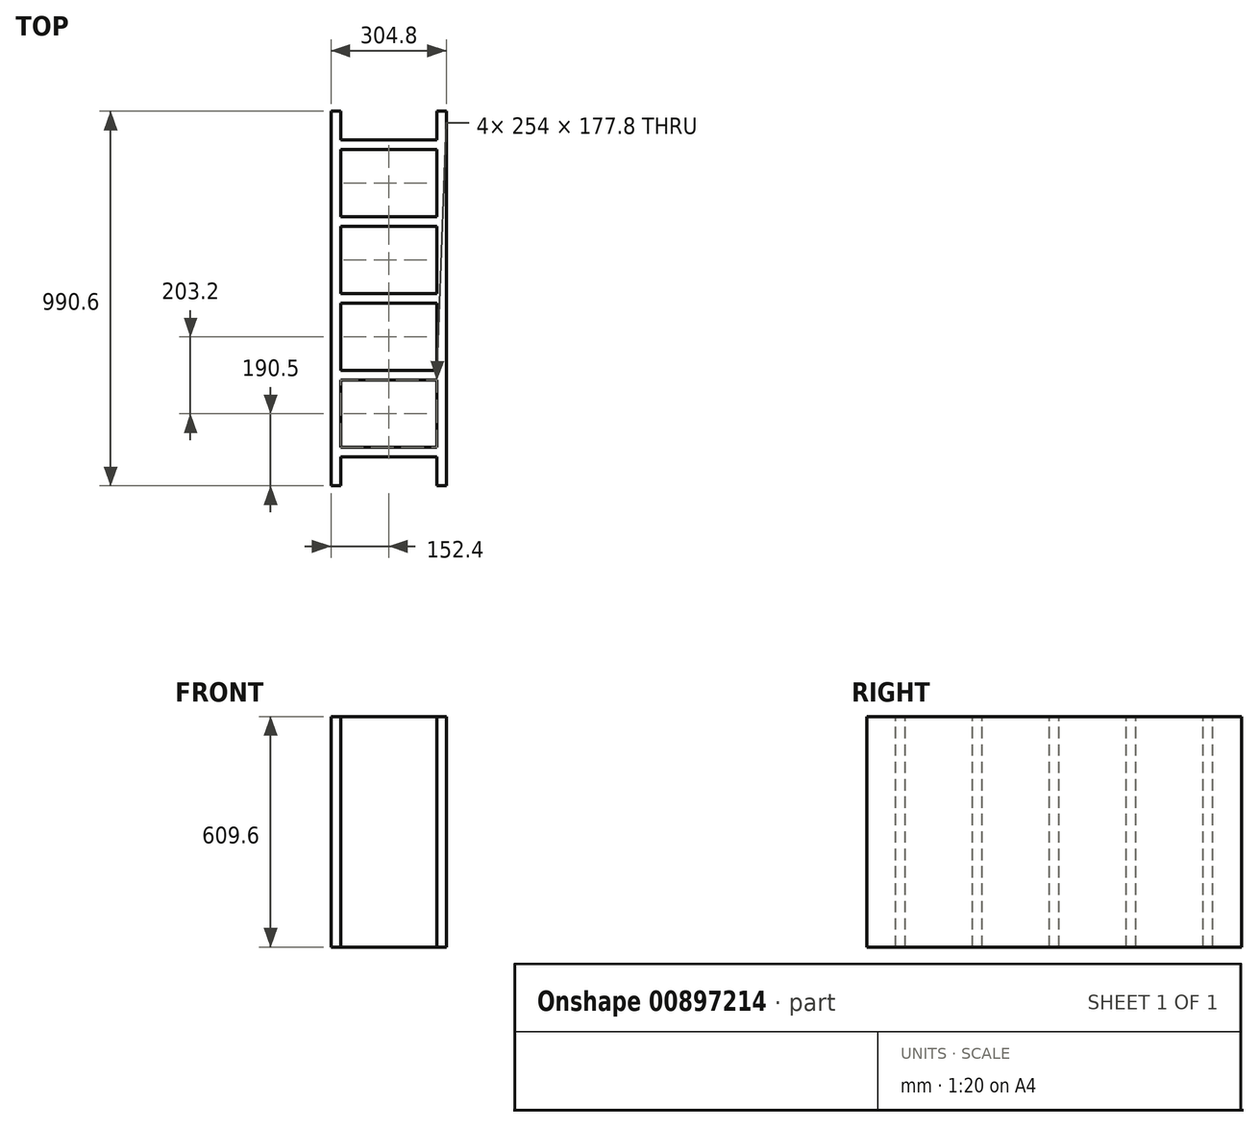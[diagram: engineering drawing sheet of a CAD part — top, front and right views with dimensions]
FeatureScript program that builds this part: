
annotation { "Feature Type Name" : "Feature", "Feature Type Description" : "" }
export const myFeature = defineFeature(function(context is Context, id is Id, definition is map)
    precondition{}
    {
        {
            var Q0;
            Q0=qCreatedBy(makeId("Top.planeOp"),FACE);
            var sketch = newSketch(context, id + "F0", { "sketchPlane" : qUnion([Q0])});
            skLineSegment(sketch, "E0.top", {"start": v(0, 838.2) * mm, "end": v(304.8, 838.2) * mm});
            skLineSegment(sketch, "E0.left", {"start": v(0, 419.1) * mm, "end": v(0, 838.2) * mm});
            skLineSegment(sketch, "E0.right", {"start": v(304.8, 419.1) * mm, "end": v(304.8, 431.8) * mm});
            skLineSegment(sketch, "E1", {"start": v(25.4, 812.8) * mm, "end": v(304.8, 812.8) * mm});
            skLineSegment(sketch, "E2", {"start": v(0, 419.1) * mm, "end": v(416.46, 419.1) * mm, "construction": true});
            skLineSegment(sketch, "E3", {"start": v(25.4, 812.8) * mm, "end": v(25.4, 635) * mm});
            skLineSegment(sketch, "E4", {"start": v(25.4, 431.8) * mm, "end": v(304.8, 431.8) * mm});
            skPoint(sketch, "E0.bottom.start.orphan", {"position": v(0, 0) * mm});
            skLineSegment(sketch, "E5.trimOffspring", {"start": v(304.8, 812.8) * mm, "end": v(304.8, 838.2) * mm});
            skLineSegment(sketch, "E6.MirrorCS", {"start": v(304.8, 25.4) * mm, "end": v(304.8, 0) * mm});
            skLineSegment(sketch, "E7.MirrorCS", {"start": v(304.8, 419.1) * mm, "end": v(304.8, 406.4) * mm});
            skLineSegment(sketch, "E8.MirrorCS", {"start": v(25.4, 25.4) * mm, "end": v(304.8, 25.4) * mm});
            skLineSegment(sketch, "E9.MirrorCS", {"start": v(0, 0) * mm, "end": v(304.8, 0) * mm});
            skLineSegment(sketch, "E10.MirrorCS", {"start": v(25.4, 406.4) * mm, "end": v(304.8, 406.4) * mm});
            skLineSegment(sketch, "E11.MirrorCS", {"start": v(25.4, 25.4) * mm, "end": v(25.4, 203.2) * mm});
            skLineSegment(sketch, "E12.MirrorCS", {"start": v(0, 419.1) * mm, "end": v(0, 0) * mm});
            skPoint(sketch, "E13.orphan", {"position": v(25.4, 419.1) * mm});
            skLineSegment(sketch, "E14.0.1.0", {"start": v(25.4, 635) * mm, "end": v(304.8, 635) * mm});
            skLineSegment(sketch, "E14.0.1.1", {"start": v(304.8, 622.3) * mm, "end": v(304.8, 635) * mm});
            skLineSegment(sketch, "E14.0.1.2", {"start": v(304.8, 622.3) * mm, "end": v(304.8, 609.6) * mm});
            skLineSegment(sketch, "E14.0.1.3", {"start": v(25.4, 609.6) * mm, "end": v(304.8, 609.6) * mm});
            skLineSegment(sketch, "E14.direction1", {"start": v(25.4, 431.8) * mm, "end": v(50.8, 431.8) * mm, "construction": true});
            skLineSegment(sketch, "E14.direction2", {"start": v(25.4, 431.8) * mm, "end": v(25.4, 609.6) * mm, "construction": true});
            skLineSegment(sketch, "E15.trimOffspring", {"start": v(25.4, 609.6) * mm, "end": v(25.4, 431.8) * mm});
            skLineSegment(sketch, "E16.MirrorCS", {"start": v(25.4, 203.2) * mm, "end": v(304.8, 203.2) * mm});
            skLineSegment(sketch, "E17.MirrorCS", {"start": v(25.4, 228.6) * mm, "end": v(304.8, 228.6) * mm});
            skLineSegment(sketch, "E18.MirrorCS", {"start": v(304.8, 215.9) * mm, "end": v(304.8, 203.2) * mm});
            skLineSegment(sketch, "E19.MirrorCS", {"start": v(304.8, 215.9) * mm, "end": v(304.8, 228.6) * mm});
            skLineSegment(sketch, "E20.trimOffspring", {"start": v(25.4, 228.6) * mm, "end": v(25.4, 406.4) * mm});
            skSolve(sketch);
        }
        {
            var Q0;
            Q0 = qSketchRegion(id + "F0", true);
            extrude(context, id + "F1", {"entities" : qUnion([Q0]), "oppositeDirection" : true, "depth" : 609.6 * mm, "offsetDistance" : 25.4 * mm});
        }
        {
            var Q0;
            Q0=makeQuery(id+"F0.imprint","IMPRINT",FACE,{"disambiguationData":[TD([[makeQuery(id+"F0.imprint","IMPRINT",EDGE,{"derivedFrom":sQuery(id+"F0.wireOp",EDGE,"E0.top")}),-1.0]])]});
            var sketch = newSketch(context, id + "F2", { "sketchPlane" : qUnion([Q0])});
            skLineSegment(sketch, "E21.bottom", {"start": v(0, 838.2) * mm, "end": v(25.4, 838.2) * mm});
            skLineSegment(sketch, "E21.top", {"start": v(0, 914.4) * mm, "end": v(25.4, 914.4) * mm});
            skLineSegment(sketch, "E21.left", {"start": v(0, 838.2) * mm, "end": v(0, 914.4) * mm});
            skLineSegment(sketch, "E21.right", {"start": v(25.4, 838.2) * mm, "end": v(25.4, 914.4) * mm});
            skLineSegment(sketch, "E22.MirrorCS", {"start": v(0, -76.2) * mm, "end": v(25.4, -76.2) * mm});
            skLineSegment(sketch, "E23.MirrorCS", {"start": v(0, 0) * mm, "end": v(0, -76.2) * mm});
            skLineSegment(sketch, "E24.MirrorCS", {"start": v(0, 0) * mm, "end": v(25.4, 0) * mm});
            skLineSegment(sketch, "E25.MirrorCS", {"start": v(25.4, 0) * mm, "end": v(25.4, -76.2) * mm});
            skLineSegment(sketch, "E26.bottom", {"start": v(304.8, 838.2) * mm, "end": v(279.4, 838.2) * mm});
            skLineSegment(sketch, "E26.top", {"start": v(304.8, 0) * mm, "end": v(279.4, 0) * mm});
            skLineSegment(sketch, "E26.left", {"start": v(304.8, 838.2) * mm, "end": v(304.8, 0) * mm});
            skLineSegment(sketch, "E26.right", {"start": v(279.4, 838.2) * mm, "end": v(279.4, 0) * mm});
            skLineSegment(sketch, "E27.top", {"start": v(304.8, 914.4) * mm, "end": v(279.4, 914.4) * mm});
            skLineSegment(sketch, "E27.left", {"start": v(304.8, 838.2) * mm, "end": v(304.8, 914.4) * mm});
            skLineSegment(sketch, "E27.right", {"start": v(279.4, 838.2) * mm, "end": v(279.4, 914.4) * mm});
            skLineSegment(sketch, "E28.MirrorCS", {"start": v(304.8, 0) * mm, "end": v(304.8, -76.2) * mm});
            skLineSegment(sketch, "E29.MirrorCS", {"start": v(279.4, 0) * mm, "end": v(279.4, -76.2) * mm});
            skLineSegment(sketch, "E30.MirrorCS", {"start": v(304.8, -76.2) * mm, "end": v(279.4, -76.2) * mm});
            skSolve(sketch);
        }
        {
            var Q0;
            Q0 = qSketchRegion(id + "F2", true);
            extrude(context, id + "F3", {"entities" : qUnion([Q0]), "operationType" : NewBodyOperationType.ADD, "oppositeDirection" : true, "depth" : 609.6 * mm, "offsetDistance" : 25.4 * mm});
        }
    });
